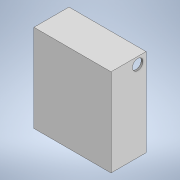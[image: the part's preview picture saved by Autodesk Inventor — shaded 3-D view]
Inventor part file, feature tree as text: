
AUTODESK INVENTOR PART (.ipt)
format: ipt  version: 2020 (Build 240168000, 168)  size: 116,736 bytes
history: native  units: mm
features: extrude x3, sketch x3
ambient origin geometry x8: Origin, YZ Plane, XZ Plane, XY Plane, X Axis, Y Axis, Z Axis, Center Point
bodies: Solid1 (feature_tree)
feature tree (6):
  extrude  "Extrusion1"  Depth=250.0mm
  extrude  "Extrusion2"  Depth=210.0mm
  extrude  "Extrusion3"  Depth=95.0mm TaperAngle=0.0deg
  sketch  "Sketch1"  dims[d0=220.0mm d1=250.0mm]
  sketch  "Sketch2"  dims[d2=100.0mm d3=0.0mm d4=210.0mm]
  sketch  "Sketch3"  dims[d5=240.0mm d6=95.0mm d7=0.0mm d8=5.0mm d9=30.0mm d10=20.0mm d11=45.0mm d12=0.0mm d13=5.0mm]
